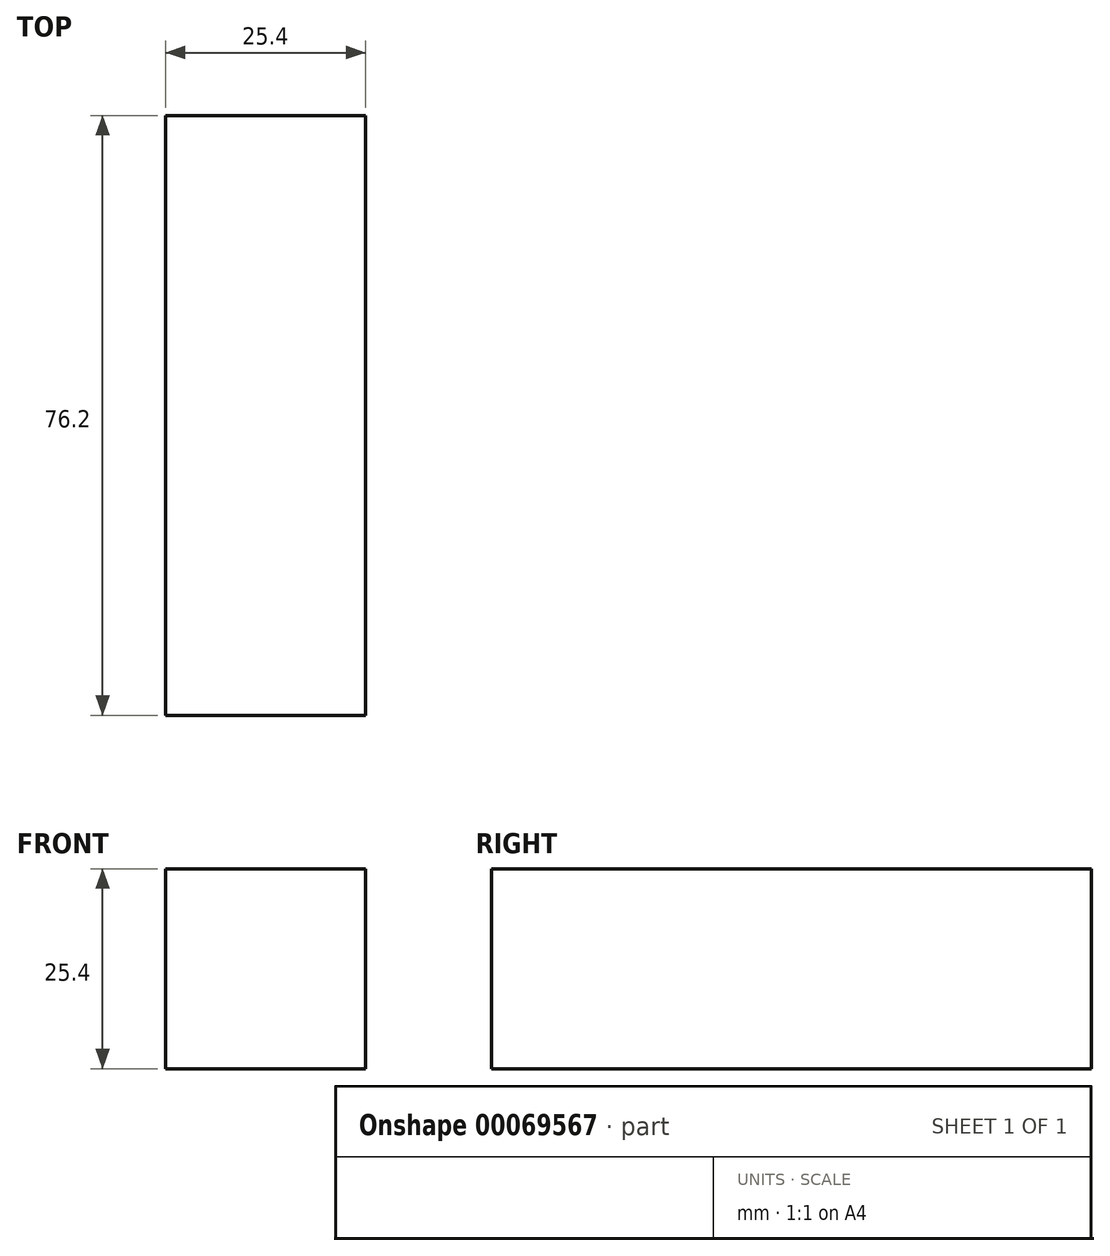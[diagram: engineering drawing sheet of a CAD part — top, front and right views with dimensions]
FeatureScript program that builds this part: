
annotation { "Feature Type Name" : "Feature", "Feature Type Description" : "" }
export const myFeature = defineFeature(function(context is Context, id is Id, definition is map)
    precondition{}
    {
        {
            var Q0;
            Q0=qCreatedBy(makeId("Front.planeOp"),FACE);
            var sketch = newSketch(context, id + "F0", { "sketchPlane" : qUnion([Q0])});
            skLineSegment(sketch, "E0.bottom", {"start": v(0, 0) * mm, "end": v(-25.4, 0) * mm});
            skLineSegment(sketch, "E0.top", {"start": v(0, 25.4) * mm, "end": v(-25.4, 25.4) * mm});
            skLineSegment(sketch, "E0.left", {"start": v(0, 0) * mm, "end": v(0, 25.4) * mm});
            skLineSegment(sketch, "E0.right", {"start": v(-25.4, 0) * mm, "end": v(-25.4, 25.4) * mm});
            skSolve(sketch);
        }
        {
            var Q0;
            Q0=makeQuery(id+"F0.imprint","IMPRINT",FACE,{"disambiguationData":[TD([[makeQuery(id+"F0.imprint","IMPRINT",EDGE,{"derivedFrom":sQuery(id+"F0.wireOp",EDGE,"E0.bottom")}),-1.0]])]});
            extrude(context, id + "F1", {"entities" : qUnion([Q0]), "endBound" : BoundingType.SYMMETRIC, "depth" : 76.2 * mm});
        }
    });
